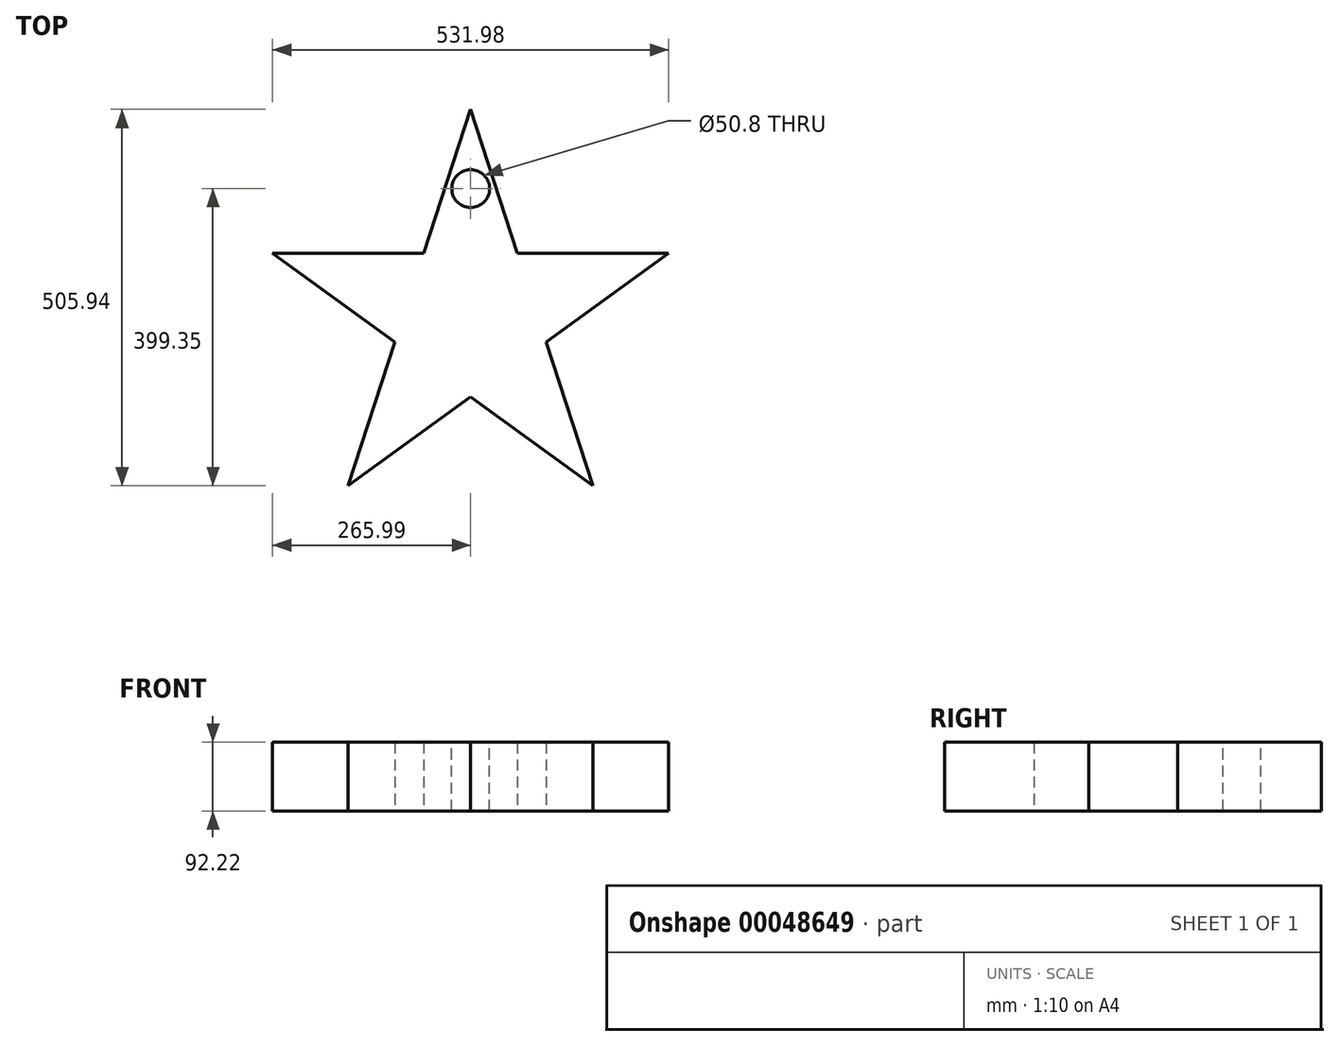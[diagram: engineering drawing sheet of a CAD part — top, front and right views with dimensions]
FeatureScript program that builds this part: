
annotation { "Feature Type Name" : "Feature", "Feature Type Description" : "" }
export const myFeature = defineFeature(function(context is Context, id is Id, definition is map)
    precondition{}
    {
        {
            var Q0;
            Q0=qCreatedBy(makeId("Top.planeOp"),FACE);
            var sketch = newSketch(context, id + "F0", { "sketchPlane" : qUnion([Q0])});
            skLineSegment(sketch, "E0", {"start": v(0, 302.05) * mm, "end": v(62.8, 108.8) * mm});
            skLineSegment(sketch, "E1", {"start": v(62.8, 108.8) * mm, "end": v(266, 108.8) * mm});
            skLineSegment(sketch, "E2", {"start": v(0, 302.05) * mm, "end": v(-62.8, 108.8) * mm});
            skLineSegment(sketch, "E3", {"start": v(-62.8, 108.8) * mm, "end": v(-266, 108.8) * mm});
            skLineSegment(sketch, "E4", {"start": v(-266, 108.8) * mm, "end": v(-101.6, -10.64) * mm});
            skLineSegment(sketch, "E5", {"start": v(-101.6, -10.64) * mm, "end": v(-164.4, -203.9) * mm});
            skLineSegment(sketch, "E6", {"start": v(-164.4, -203.9) * mm, "end": v(0, -84.46) * mm});
            skLineSegment(sketch, "E7", {"start": v(0, -84.46) * mm, "end": v(164.4, -203.9) * mm});
            skLineSegment(sketch, "E8", {"start": v(164.4, -203.9) * mm, "end": v(101.6, -10.64) * mm});
            skLineSegment(sketch, "E9", {"start": v(266, 108.8) * mm, "end": v(101.6, -10.64) * mm});
            skSolve(sketch);
        }
        {
            var Q0;
            Q0=makeQuery(id+"F0.imprint","IMPRINT",FACE,{"disambiguationData":[TD([[makeQuery(id+"F0.imprint","IMPRINT",EDGE,{"derivedFrom":sQuery(id+"F0.wireOp",EDGE,"E0")}),-1.0]])]});
            extrude(context, id + "F1", {"entities" : qUnion([Q0]), "depth" : 92.22 * mm});
        }
        {
            var Q0;
            Q0=makeQuery(id+"F1.opExtrude","CAP_FACE",FACE,{"disambiguationData":[OSD([sQuery(id+"F0.wireOp",EDGE,"E0"),sQuery(id+"F0.wireOp",EDGE,"E1"),sQuery(id+"F0.wireOp",EDGE,"E2"),sQuery(id+"F0.wireOp",EDGE,"E3"),sQuery(id+"F0.wireOp",EDGE,"E4"),sQuery(id+"F0.wireOp",EDGE,"E5"),sQuery(id+"F0.wireOp",EDGE,"E6"),sQuery(id+"F0.wireOp",EDGE,"E7"),sQuery(id+"F0.wireOp",EDGE,"E8"),sQuery(id+"F0.wireOp",EDGE,"E9")])],"isStart":false});
            var sketch = newSketch(context, id + "F2", { "sketchPlane" : qUnion([Q0])});
            skCircle(sketch, "E10", {"center": v(0, 195.46) * mm, "radius": 25.4 * mm});
            skSolve(sketch);
        }
        {
            var Q0;
            Q0=makeQuery(id+"F2.imprint","IMPRINT",FACE,{"disambiguationData":[TD([[makeQuery(id+"F2.imprint","IMPRINT",EDGE,{"derivedFrom":sQuery(id+"F2.wireOp",EDGE,"E10")}),1.0]])]});
            extrude(context, id + "F3", {"entities" : qUnion([Q0]), "operationType" : NewBodyOperationType.REMOVE, "oppositeDirection" : true, "depth" : 267.25 * mm});
        }
    });
